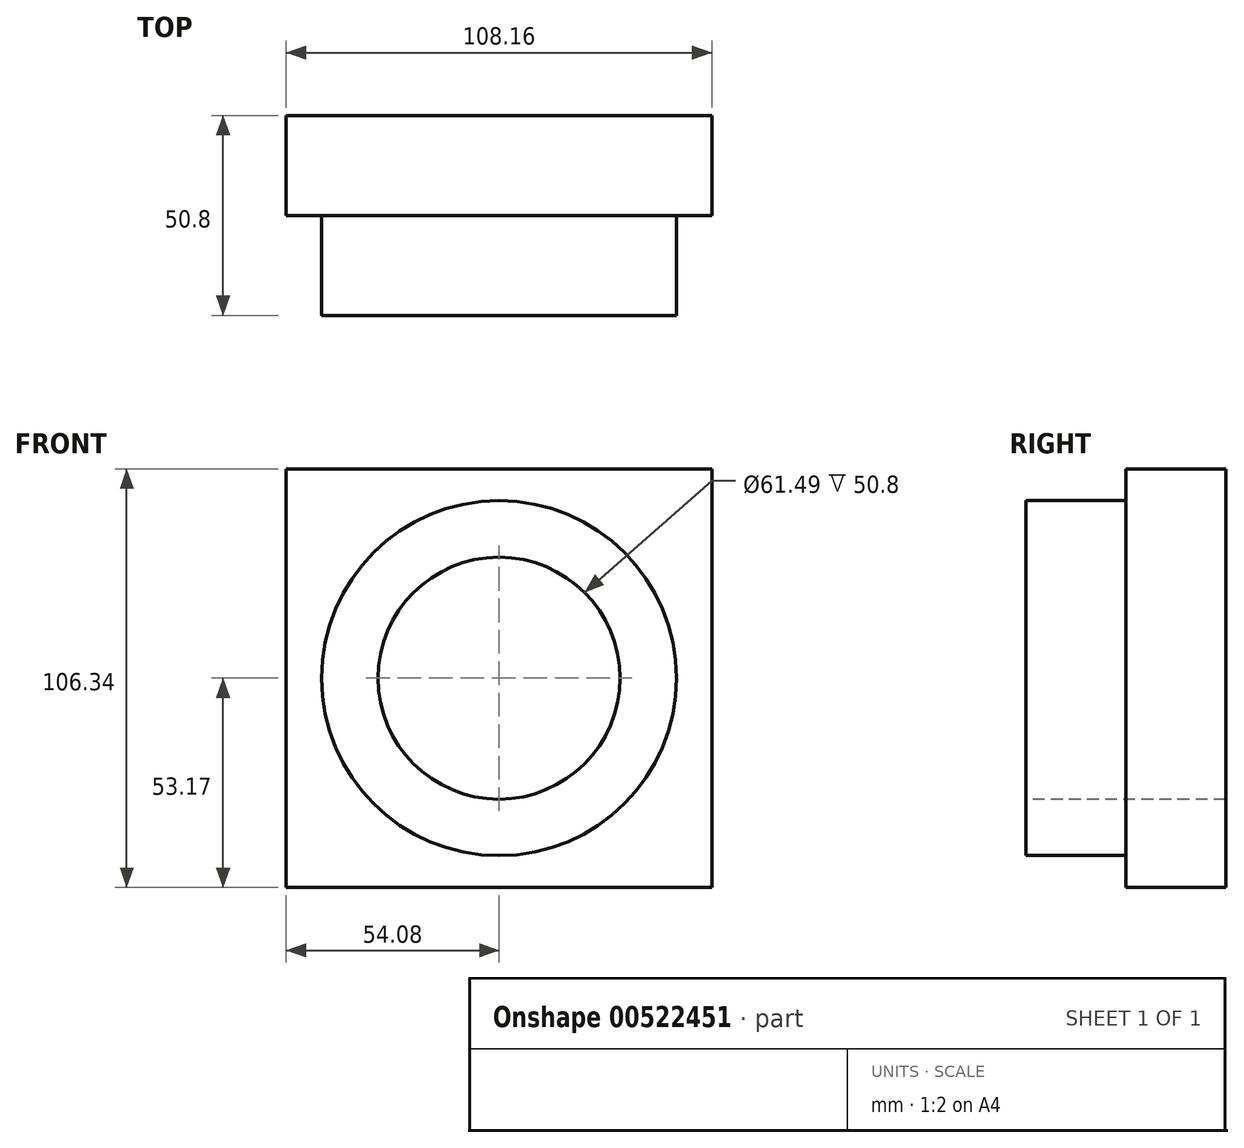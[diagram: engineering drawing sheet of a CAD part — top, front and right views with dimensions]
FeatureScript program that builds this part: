
annotation { "Feature Type Name" : "Feature", "Feature Type Description" : "" }
export const myFeature = defineFeature(function(context is Context, id is Id, definition is map)
    precondition{}
    {
        {
            var Q0;
            Q0=qCreatedBy(makeId("Front.planeOp"),FACE);
            var sketch = newSketch(context, id + "F0", { "sketchPlane" : qUnion([Q0])});
            skLineSegment(sketch, "E0.bottom", {"start": v(54.08, -53.17) * mm, "end": v(-54.08, -53.17) * mm});
            skLineSegment(sketch, "E0.top", {"start": v(54.08, 53.17) * mm, "end": v(-54.08, 53.17) * mm});
            skLineSegment(sketch, "E0.left", {"start": v(54.08, -53.17) * mm, "end": v(54.08, 53.17) * mm});
            skLineSegment(sketch, "E0.right", {"start": v(-54.08, -53.17) * mm, "end": v(-54.08, 53.17) * mm});
            skPoint(sketch, "E0.middle", {"position": v(0, 0) * mm});
            skSolve(sketch);
        }
        {
            var Q0;
            Q0 = qSketchRegion(id + "F0", true);
            extrude(context, id + "F1", {"entities" : qUnion([Q0]), "depth" : 25.4 * mm, "offsetDistance" : 25.4 * mm});
        }
        {
            var Q0;
            Q0=makeQuery(id+"F1.opExtrude","CAP_FACE",FACE,{"disambiguationData":[OSD([sQuery(id+"F0.wireOp",EDGE,"E0.bottom"),sQuery(id+"F0.wireOp",EDGE,"E0.top"),sQuery(id+"F0.wireOp",EDGE,"E0.left"),sQuery(id+"F0.wireOp",EDGE,"E0.right")])],"isStart":false});
            var sketch = newSketch(context, id + "F2", { "sketchPlane" : qUnion([Q0])});
            skCircle(sketch, "E1", {"center": v(0, 0) * mm, "radius": 41.56 * mm});
            skCircle(sketch, "E2", {"center": v(0, 0) * mm, "radius": 30.74 * mm});
            skSolve(sketch);
        }
        {
            var Q0;
            Q0=makeQuery(id+"F2.imprint","IMPRINT",FACE,{"disambiguationData":[TD([[makeQuery(id+"F2.imprint","IMPRINT",EDGE,{"derivedFrom":sQuery(id+"F2.wireOp",EDGE,"E2")}),1.0]])]});
            var Q1;
            Q1=sQuery(id+"F2.wireOp",EDGE,"E2");
            extrude(context, id + "F3", {"entities" : qUnion([Q0]), "operationType" : NewBodyOperationType.REMOVE, "surfaceEntities" : qUnion([Q1]), "endBound" : BoundingType.THROUGH_ALL, "oppositeDirection" : true, "depth" : 25.4 * mm, "offsetDistance" : 25.4 * mm});
        }
        {
            var Q0;
            Q0=makeQuery(id+"F1.opExtrude","CAP_FACE",FACE,{"disambiguationData":[OSD([sQuery(id+"F0.wireOp",EDGE,"E0.bottom"),sQuery(id+"F0.wireOp",EDGE,"E0.top"),sQuery(id+"F0.wireOp",EDGE,"E0.left"),sQuery(id+"F0.wireOp",EDGE,"E0.right")])],"isStart":false});
            var sketch = newSketch(context, id + "F4", { "sketchPlane" : qUnion([Q0])});
            skCircle(sketch, "E3", {"center": v(0, 0) * mm, "radius": 45.09 * mm});
            skSolve(sketch);
        }
        {
            var Q0;
            Q0=makeQuery(id+"F4.imprint","IMPRINT",FACE,{"disambiguationData":[TD([[makeQuery(id+"F4.imprint","IMPRINT",EDGE,{"derivedFrom":sQuery(id+"F4.wireOp",EDGE,"E3")}),1.0]])]});
            extrude(context, id + "F5", {"entities" : qUnion([Q0]), "operationType" : NewBodyOperationType.ADD, "depth" : 25.4 * mm, "offsetDistance" : 25.4 * mm});
        }
    });
